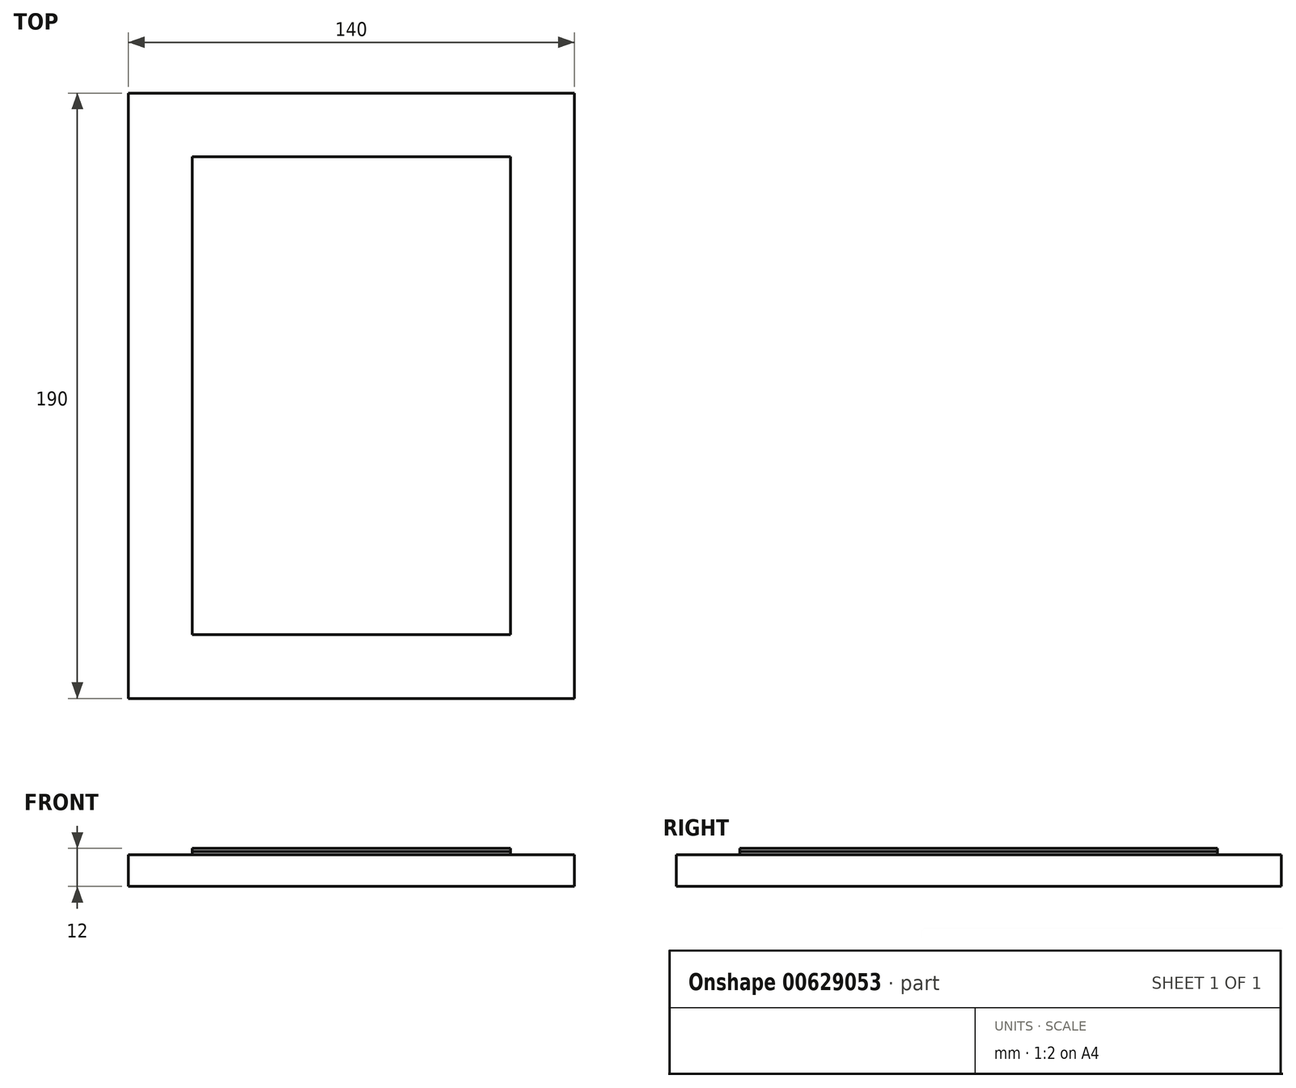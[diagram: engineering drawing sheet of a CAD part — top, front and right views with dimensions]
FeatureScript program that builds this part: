
annotation { "Feature Type Name" : "Feature", "Feature Type Description" : "" }
export const myFeature = defineFeature(function(context is Context, id is Id, definition is map)
    precondition{}
    {
        {
            var Q0;
            Q0=qCreatedBy(makeId("Top.planeOp"),FACE);
            var sketch = newSketch(context, id + "F0", { "sketchPlane" : qUnion([Q0])});
            skLineSegment(sketch, "E0.bottom", {"start": v(-50, 75) * mm, "end": v(50, 75) * mm});
            skLineSegment(sketch, "E0.top", {"start": v(-50, -75) * mm, "end": v(50, -75) * mm});
            skLineSegment(sketch, "E0.left", {"start": v(-50, 75) * mm, "end": v(-50, -75) * mm});
            skLineSegment(sketch, "E0.right", {"start": v(50, 75) * mm, "end": v(50, -75) * mm});
            skLineSegment(sketch, "E1.bottom", {"start": v(-70, 95) * mm, "end": v(70, 95) * mm});
            skLineSegment(sketch, "E1.top", {"start": v(-70, -95) * mm, "end": v(70, -95) * mm});
            skLineSegment(sketch, "E1.left", {"start": v(-70, 95) * mm, "end": v(-70, -95) * mm});
            skLineSegment(sketch, "E1.right", {"start": v(70, 95) * mm, "end": v(70, -95) * mm});
            skSolve(sketch);
        }
        {
            var Q0;
            Q0=makeQuery(id+"F0.imprint","IMPRINT",FACE,{"disambiguationData":[TD([[makeQuery(id+"F0.imprint","IMPRINT",EDGE,{"derivedFrom":sQuery(id+"F0.wireOp",EDGE,"E0.bottom")}),-1.0]])]});
            extrude(context, id + "F1", {"entities" : qUnion([Q0]), "depth" : 11 * mm, "offsetDistance" : 25 * mm});
        }
        {
            var Q0;
            Q0=makeQuery(id+"F0.imprint","IMPRINT",FACE,{"disambiguationData":[TD([[makeQuery(id+"F0.imprint","IMPRINT",EDGE,{"derivedFrom":sQuery(id+"F0.wireOp",EDGE,"E0.bottom")}),1.0]])]});
            extrude(context, id + "F2", {"entities" : qUnion([Q0]), "operationType" : NewBodyOperationType.ADD, "depth" : 10 * mm, "offsetDistance" : 25 * mm});
        }
        {
            var Q0;
            Q0=makeQuery(id+"F1.opExtrude","CAP_FACE",FACE,{"disambiguationData":[OSD([sQuery(id+"F0.wireOp",EDGE,"E0.bottom"),sQuery(id+"F0.wireOp",EDGE,"E0.top"),sQuery(id+"F0.wireOp",EDGE,"E0.left"),sQuery(id+"F0.wireOp",EDGE,"E0.right")])],"isStart":false});
            extrude(context, id + "F3", {"entities" : qUnion([Q0]), "depth" : 1 * mm, "offsetDistance" : 25 * mm});
        }
    });
